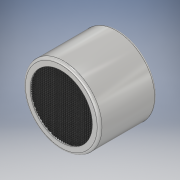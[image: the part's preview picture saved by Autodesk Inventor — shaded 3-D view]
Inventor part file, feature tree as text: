
AUTODESK INVENTOR PART (.ipt)
format: ipt  version: 2019.4 (Build 234330000, 330)  size: 5,357,568 bytes
history: native  units: mm
features: sketch x5, extrude x4, other x3, fillet x2
ambient origin geometry x8: Origin, YZ Plane, XZ Plane, XY Plane, X Axis, Y Axis, Z Axis, Center Point
bodies: Solide1 (feature_tree)
feature tree (14):
  extrude  "Extrusion1"  Depth=16.0mm
  fillet  "Congé1"  Radius=12.0mm
  extrude  "Extrusion2"  Depth=0.5mm
  other  "Plan de construction1"
  fillet  "Congé2"  Radius=13.0mm
  extrude  "Extrusion3"  Depth=10.0mm TaperAngle=0.0deg
  other  "Révolution1"
  other  "Plan de construction2"
  extrude  "Extrusion4"  Depth=0.5mm
  sketch  "Esquisse1"
  sketch  "Esquisse2"
  sketch  "Esquisse3"
  sketch  "Esquisse4"
  sketch  "Esquisse5"
